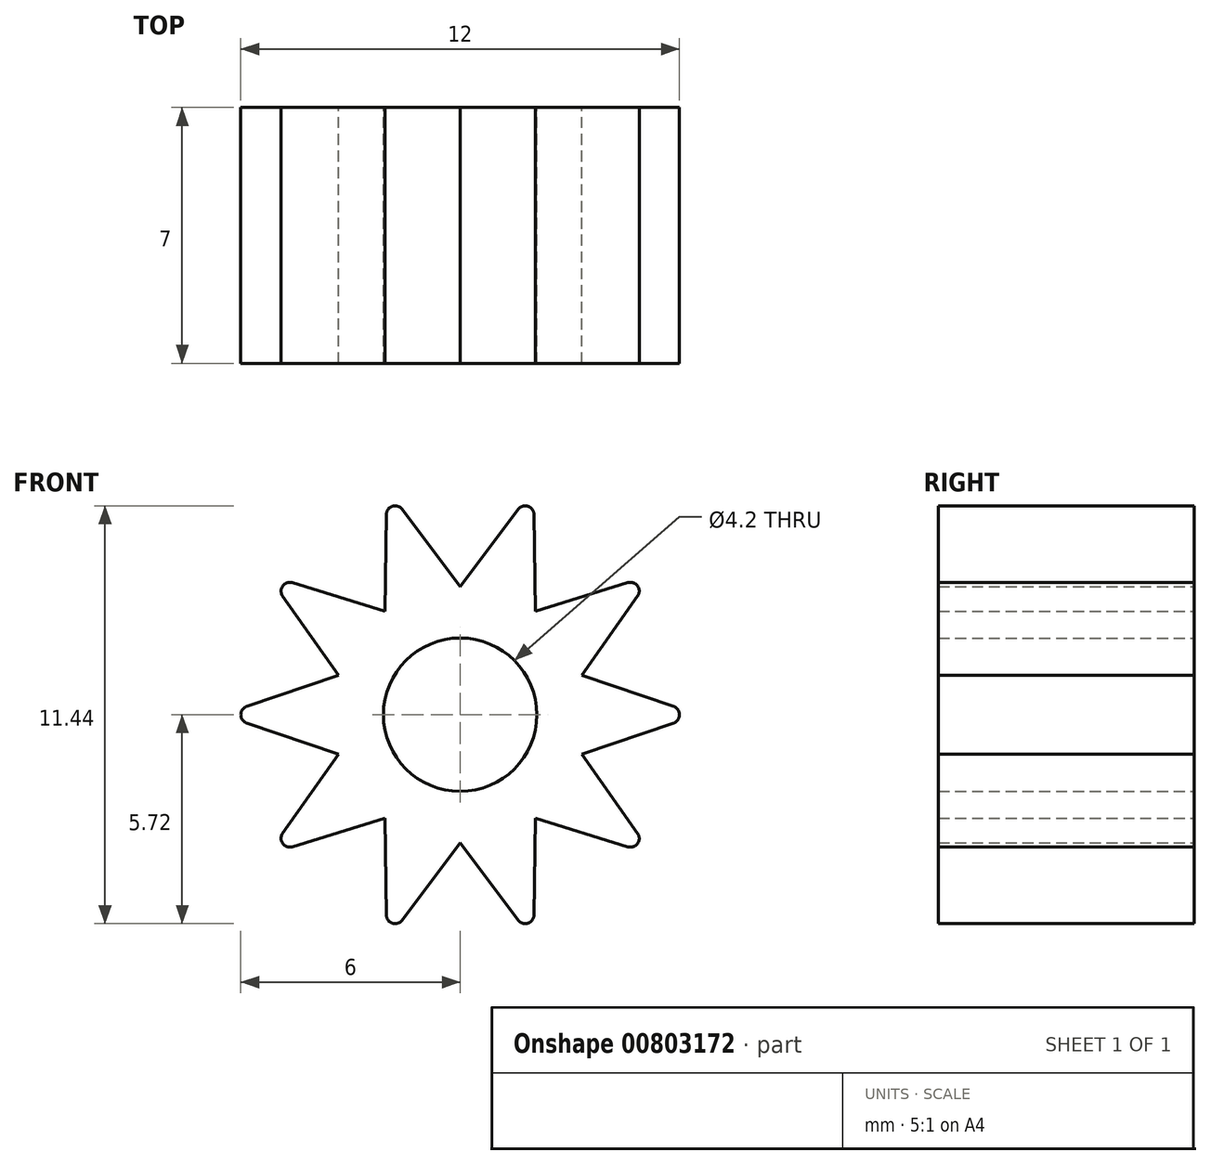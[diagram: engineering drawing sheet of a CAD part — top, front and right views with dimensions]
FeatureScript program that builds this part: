
annotation { "Feature Type Name" : "Feature", "Feature Type Description" : "" }
export const myFeature = defineFeature(function(context is Context, id is Id, definition is map)
    precondition{}
    {
        {
            var Q0;
            Q0=qCreatedBy(makeId("Front.planeOp"),FACE);
            var sketch = newSketch(context, id + "F0", { "sketchPlane" : qUnion([Q0])});
            skCircle(sketch, "E0", {"center": v(0, 0) * mm, "radius": 2.1 * mm});
            skCircle(sketch, "E1", {"center": v(0, 0) * mm, "radius": 6.5 * mm});
            skLineSegment(sketch, "E2", {"start": v(-1.59, 5.62) * mm, "end": v(0, 3.5) * mm});
            skLineSegment(sketch, "E3", {"start": v(0, 3.5) * mm, "end": v(2, 6.18) * mm});
            skLineSegment(sketch, "E4.1.0", {"start": v(-2.06, 2.83) * mm, "end": v(-2.02, 5.48) * mm});
            skLineSegment(sketch, "E4.1.1", {"start": v(-5.26, 3.82) * mm, "end": v(-2.06, 2.83) * mm});
            skLineSegment(sketch, "E4.2.0", {"start": v(-3.33, 1.08) * mm, "end": v(-5.26, 3.82) * mm});
            skLineSegment(sketch, "E4.2.1", {"start": v(-6.5, 0) * mm, "end": v(-3.33, 1.08) * mm});
            skLineSegment(sketch, "E5.1.3.0", {"start": v(-3.33, -1.08) * mm, "end": v(-6.5, 0) * mm});
            skLineSegment(sketch, "E5.3.3.0", {"start": v(-5.26, -3.82) * mm, "end": v(-3.33, -1.08) * mm});
            skLineSegment(sketch, "E5.1.4.0", {"start": v(-2.06, -2.83) * mm, "end": v(-5.26, -3.82) * mm});
            skLineSegment(sketch, "E5.3.4.0", {"start": v(-2, -6.18) * mm, "end": v(-2.06, -2.83) * mm});
            skLineSegment(sketch, "E6.1.5.0", {"start": v(0, -3.5) * mm, "end": v(-2, -6.18) * mm});
            skLineSegment(sketch, "E6.3.5.0", {"start": v(2, -6.18) * mm, "end": v(0, -3.5) * mm});
            skLineSegment(sketch, "E6.1.6.0", {"start": v(2.06, -2.83) * mm, "end": v(2, -6.18) * mm});
            skLineSegment(sketch, "E6.3.6.0", {"start": v(5.26, -3.82) * mm, "end": v(2.06, -2.83) * mm});
            skLineSegment(sketch, "E6.1.7.0", {"start": v(3.33, -1.08) * mm, "end": v(5.26, -3.82) * mm});
            skLineSegment(sketch, "E6.3.7.0", {"start": v(6.5, 0) * mm, "end": v(3.33, -1.08) * mm});
            skLineSegment(sketch, "E6.1.8.0", {"start": v(3.33, 1.08) * mm, "end": v(6.5, 0) * mm});
            skLineSegment(sketch, "E6.3.8.0", {"start": v(5.26, 3.82) * mm, "end": v(3.33, 1.08) * mm});
            skLineSegment(sketch, "E6.1.9.0", {"start": v(2.06, 2.83) * mm, "end": v(5.26, 3.82) * mm});
            skLineSegment(sketch, "E6.3.9.0", {"start": v(2, 6.18) * mm, "end": v(2.06, 2.83) * mm});
            skCircle(sketch, "E7", {"center": v(0, 0) * mm, "radius": 2 * mm});
            skPoint(sketch, "E8.visualSharp", {"position": v(-2, 6.18) * mm});
            skArc(sketch, "E8.filletArc", {"start": v(-1.59, 5.62) * mm, "mid": v(-1.85, 5.7) * mm, "end": v(-2.02, 5.48) * mm});
            skCircle(sketch, "E9", {"center": v(0, 0) * mm, "radius": 6 * mm, "construction": true});
            skPoint(sketch, "E10", {"position": v(-1.85, 5.7) * mm});
            skArc(sketch, "E11.1.0", {"start": v(-4.6, 3.61) * mm, "mid": v(-4.85, 3.53) * mm, "end": v(-4.86, 3.25) * mm});
            skArc(sketch, "E11.2.0", {"start": v(-5.84, 0.23) * mm, "mid": v(-6, 0) * mm, "end": v(-5.84, -0.23) * mm});
            skArc(sketch, "E11.3.0", {"start": v(-4.86, -3.25) * mm, "mid": v(-4.85, -3.53) * mm, "end": v(-4.6, -3.61) * mm});
            skArc(sketch, "E11.4.0", {"start": v(-2.02, -5.48) * mm, "mid": v(-1.85, -5.7) * mm, "end": v(-1.59, -5.62) * mm});
            skArc(sketch, "E11.5.0", {"start": v(1.59, -5.62) * mm, "mid": v(1.85, -5.7) * mm, "end": v(2.02, -5.48) * mm});
            skArc(sketch, "E11.6.0", {"start": v(4.6, -3.61) * mm, "mid": v(4.85, -3.53) * mm, "end": v(4.86, -3.25) * mm});
            skArc(sketch, "E11.7.0", {"start": v(5.84, -0.23) * mm, "mid": v(6, 0) * mm, "end": v(5.84, 0.23) * mm});
            skArc(sketch, "E11.8.0", {"start": v(4.86, 3.25) * mm, "mid": v(4.85, 3.53) * mm, "end": v(4.6, 3.61) * mm});
            skArc(sketch, "E11.9.0", {"start": v(2.02, 5.48) * mm, "mid": v(1.85, 5.7) * mm, "end": v(1.59, 5.62) * mm});
            skSolve(sketch);
        }
        {
            var Q0;
            Q0=makeQuery(id+"F0.imprint","IMPRINT",FACE,{"disambiguationData":[TD([[makeQuery(id+"F0.imprint","IMPRINT",EDGE,{"derivedFrom":sQuery(id+"F0.wireOp",EDGE,"E0")}),-1.0]])]});
            extrude(context, id + "F1", {"entities" : qUnion([Q0]), "depth" : 7 * mm, "offsetDistance" : 25 * mm});
        }
    });
